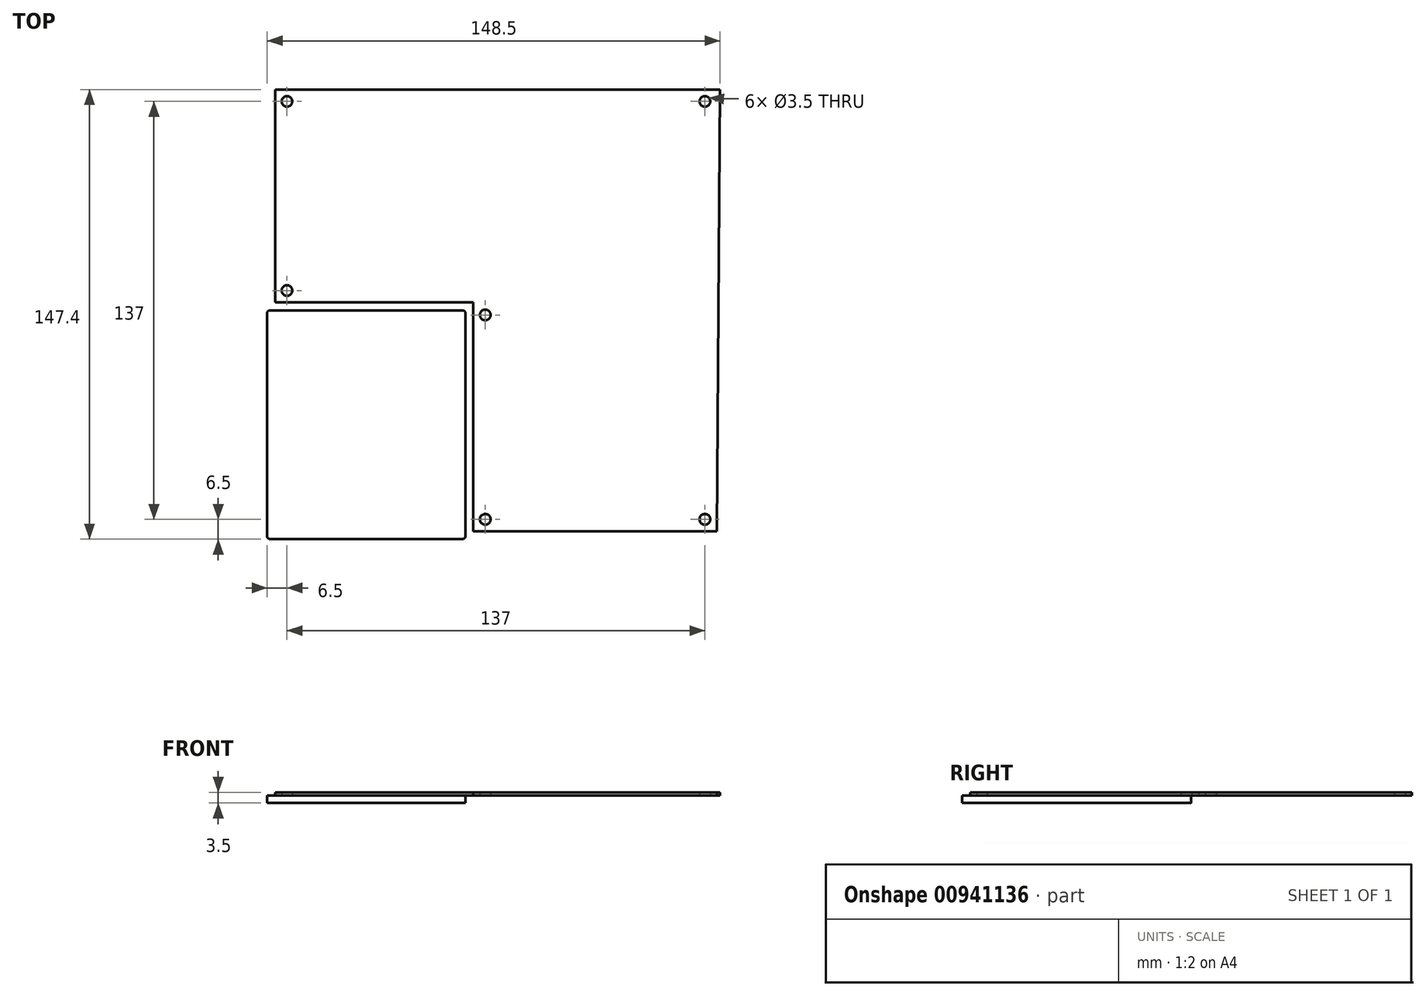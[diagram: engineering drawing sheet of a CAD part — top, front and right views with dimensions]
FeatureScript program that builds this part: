
annotation { "Feature Type Name" : "Feature", "Feature Type Description" : "" }
export const myFeature = defineFeature(function(context is Context, id is Id, definition is map)
    precondition{}
    {
        {
            var Q0;
            Q0=qCreatedBy(makeId("Top.planeOp"),FACE);
            var sketch = newSketch(context, id + "F0", { "sketchPlane" : qUnion([Q0])});
            skLineSegment(sketch, "E0.bottom", {"start": v(75, -75) * mm, "end": v(-75, -75) * mm});
            skLineSegment(sketch, "E0.top", {"start": v(75, 75) * mm, "end": v(-75, 75) * mm});
            skLineSegment(sketch, "E0.left", {"start": v(75, -75) * mm, "end": v(75, 75) * mm});
            skLineSegment(sketch, "E0.right", {"start": v(-75, -75) * mm, "end": v(-75, 75) * mm});
            skPoint(sketch, "E0.middle", {"position": v(0, 0) * mm});
            skLineSegment(sketch, "E1.bottom", {"start": v(-75, -75) * mm, "end": v(-10, -75) * mm});
            skLineSegment(sketch, "E1.top", {"start": v(-75, 0) * mm, "end": v(-10, 0) * mm});
            skLineSegment(sketch, "E1.left", {"start": v(-75, -75) * mm, "end": v(-75, 0) * mm});
            skLineSegment(sketch, "E1.right", {"start": v(-10, -75) * mm, "end": v(-10, 0) * mm});
            skSolve(sketch);
        }
        {
            var Q0;
            Q0=makeQuery(id+"F0.imprint","IMPRINT",FACE,{"disambiguationData":[TD([[makeQuery(id+"F0.imprint","IMPRINT",EDGE,{"derivedFrom":sQuery(id+"F0.wireOp",EDGE,"E0.bottom")}),-1.0]])]});
            extrude(context, id + "F1", {"entities" : qUnion([Q0]), "depth" : 2.5 * mm, "offsetDistance" : 25 * mm});
        }
        {
            var Q0;
            Q0=makeQuery(id+"F1.opExtrude","CAP_FACE",FACE,{"disambiguationData":[OSD([sQuery(id+"F0.wireOp",EDGE,"E0.bottom"),sQuery(id+"F0.wireOp",EDGE,"E0.top"),sQuery(id+"F0.wireOp",EDGE,"E0.left"),sQuery(id+"F0.wireOp",EDGE,"E0.right")])],"isStart":false});
            var sketch = newSketch(context, id + "F2", { "sketchPlane" : qUnion([Q0])});
            skCircle(sketch, "E2", {"center": v(-68.5, 68.5) * mm, "radius": 1.75 * mm});
            skCircle(sketch, "E3", {"center": v(68.5, 68.5) * mm, "radius": 1.75 * mm});
            skCircle(sketch, "E4", {"center": v(68.5, -68.5) * mm, "radius": 1.75 * mm});
            skCircle(sketch, "E5", {"center": v(-3.5, -68.5) * mm, "radius": 1.75 * mm});
            skCircle(sketch, "E6", {"center": v(-3.5, -1.5) * mm, "radius": 1.75 * mm});
            skCircle(sketch, "E7", {"center": v(-68.5, 6.5) * mm, "radius": 1.75 * mm});
            skLineSegment(sketch, "E8", {"start": v(-72.4, 72.4) * mm, "end": v(73.5, 72.4) * mm});
            skLineSegment(sketch, "E9", {"start": v(-72.4, 72.4) * mm, "end": v(-72.4, 2.6) * mm});
            skLineSegment(sketch, "E10", {"start": v(-72.4, 2.6) * mm, "end": v(-7.4, 2.6) * mm});
            skLineSegment(sketch, "E11", {"start": v(-7.4, 2.6) * mm, "end": v(-7.4, -72.4) * mm});
            skLineSegment(sketch, "E12", {"start": v(-7.4, -72.4) * mm, "end": v(72.4, -72.4) * mm});
            skLineSegment(sketch, "E13", {"start": v(73.5, 72.4) * mm, "end": v(72.4, -72.4) * mm});
            skSolve(sketch);
        }
        {
            var Q0;
            Q0=makeQuery(id+"F2.imprint","IMPRINT",FACE,{"disambiguationData":[TD([[makeQuery(id+"F2.imprint","IMPRINT",EDGE,{"derivedFrom":sQuery(id+"F2.wireOp",EDGE,"E2")}),1.0]])]});
            var Q1;
            Q1=makeQuery(id+"F2.imprint","IMPRINT",FACE,{"disambiguationData":[TD([[makeQuery(id+"F2.imprint","IMPRINT",EDGE,{"derivedFrom":sQuery(id+"F2.wireOp",EDGE,"E3")}),1.0]])]});
            var Q2;
            Q2=makeQuery(id+"F2.imprint","IMPRINT",FACE,{"disambiguationData":[TD([[makeQuery(id+"F2.imprint","IMPRINT",EDGE,{"derivedFrom":sQuery(id+"F2.wireOp",EDGE,"E4")}),1.0]])]});
            var Q3;
            Q3=makeQuery(id+"F2.imprint","IMPRINT",FACE,{"disambiguationData":[TD([[makeQuery(id+"F2.imprint","IMPRINT",EDGE,{"derivedFrom":sQuery(id+"F2.wireOp",EDGE,"E5")}),1.0]])]});
            var Q4;
            Q4=makeQuery(id+"F2.imprint","IMPRINT",FACE,{"disambiguationData":[TD([[makeQuery(id+"F2.imprint","IMPRINT",EDGE,{"derivedFrom":sQuery(id+"F2.wireOp",EDGE,"E7")}),1.0]])]});
            var Q5;
            Q5=makeQuery(id+"F2.imprint","IMPRINT",FACE,{"disambiguationData":[TD([[makeQuery(id+"F2.imprint","IMPRINT",EDGE,{"derivedFrom":sQuery(id+"F2.wireOp",EDGE,"E6")}),1.0]])]});
            extrude(context, id + "F3", {"entities" : qUnion([Q0, Q1, Q2, Q3, Q4, Q5]), "operationType" : NewBodyOperationType.REMOVE, "oppositeDirection" : true, "depth" : 3.5 * mm, "offsetDistance" : 25 * mm});
        }
        {
            var Q0;
            Q0=qSketchRegion(id+"F2",true);
            extrude(context, id + "F4", {"entities" : qUnion([Q0]), "operationType" : NewBodyOperationType.ADD, "depth" : 1 * mm, "offsetDistance" : 25 * mm});
        }
        {
            var Q0;
            Q0=makeQuery(id+"F1.opExtrude","SWEPT_EDGE",EDGE,{"disambiguationData":[OSD([sQuery(id+"F0.wireOp",EDGE,"E1.top"),sQuery(id+"F0.wireOp",EDGE,"E1.right")])]});
            var Q1;
            Q1=makeQuery(id+"F1.opExtrude","SWEPT_EDGE",EDGE,{"disambiguationData":[OSD([sQuery(id+"F0.wireOp",EDGE,"E0.bottom"),sQuery(id+"F0.wireOp",EDGE,"E1.bottom"),sQuery(id+"F0.wireOp",EDGE,"E1.right")])]});
            var Q2;
            Q2=makeQuery(id+"F1.opExtrude","SWEPT_EDGE",EDGE,{"disambiguationData":[OSD([sQuery(id+"F0.wireOp",EDGE,"E0.bottom"),sQuery(id+"F0.wireOp",EDGE,"E0.left")])]});
            var Q3;
            Q3=makeQuery(id+"F1.opExtrude","SWEPT_EDGE",EDGE,{"disambiguationData":[OSD([sQuery(id+"F0.wireOp",EDGE,"E0.top"),sQuery(id+"F0.wireOp",EDGE,"E0.left")])]});
            var Q4;
            Q4=makeQuery(id+"F1.opExtrude","SWEPT_EDGE",EDGE,{"disambiguationData":[OSD([sQuery(id+"F0.wireOp",EDGE,"E0.top"),sQuery(id+"F0.wireOp",EDGE,"E0.right")])]});
            var Q5;
            Q5=makeQuery(id+"F1.opExtrude","SWEPT_EDGE",EDGE,{"disambiguationData":[OSD([sQuery(id+"F0.wireOp",EDGE,"E0.right"),sQuery(id+"F0.wireOp",EDGE,"E1.top"),sQuery(id+"F0.wireOp",EDGE,"E1.left")])]});
            fillet(context, id + "F5", {"entities" : qUnion([Q0, Q1, Q2, Q3, Q4, Q5]), "radius" : 1 * mm, "tangentPropagation" : true, "allowEdgeOverflow" : false});
        }
    });
